# Revit family: 108P
name_source: partatom
category: Modèles génériques
units: mm (PartAtom-declared; Revit-internal decimal feet)

## family parameters
Basée sur le plan de construction = Oui
Cote de connecteur circulaire = Utiliser le diamètre
Couper avec des vides une fois chargée = Non
Numéro OmniClass = 23.85.10.11.14.14.14
Partagée = Non
Peut héberger une armature = Non
Point de calcul de pièce = Non
Titre OmniClass = Loudspeakers
Toujours verticalement = Non
Type d'élément = Normal

## types (1)
- 108P
    Amplifier power rating = LF: 1 x 500W, 8 Ω   |   HF: 1 x 260W, 8 Ω
    Cabinet = Baltic birch plywood
    Connectors = 2 x XLR in parallel   |   2 x PowerCON 120 ou 230 V selectable by switch
    Description = COAXIAL SYSTEM
    Elévation par défaut = 0 mm  [stored 0 ft]
    Fabricant = L-Acoustics
    Finish standard = L-Acoustics - Dark Grey Brown (Pantone 426C)
    Maximal SPL = 127 dB ([FILL])
    Modèle = 108P
    Transducers = LF: 1 x 8''   |    HF: 1 x 1.5''
    URL = https://www.l-acoustics.com
    Usable bandwidth (-10 dB) = 55 Hz - 22 kHz ([FRONT])
    Version = v1.0.0

note: [stored X ft] marks values corroborated as IEEE doubles in the binary element streams (Revit-internal decimal feet)
